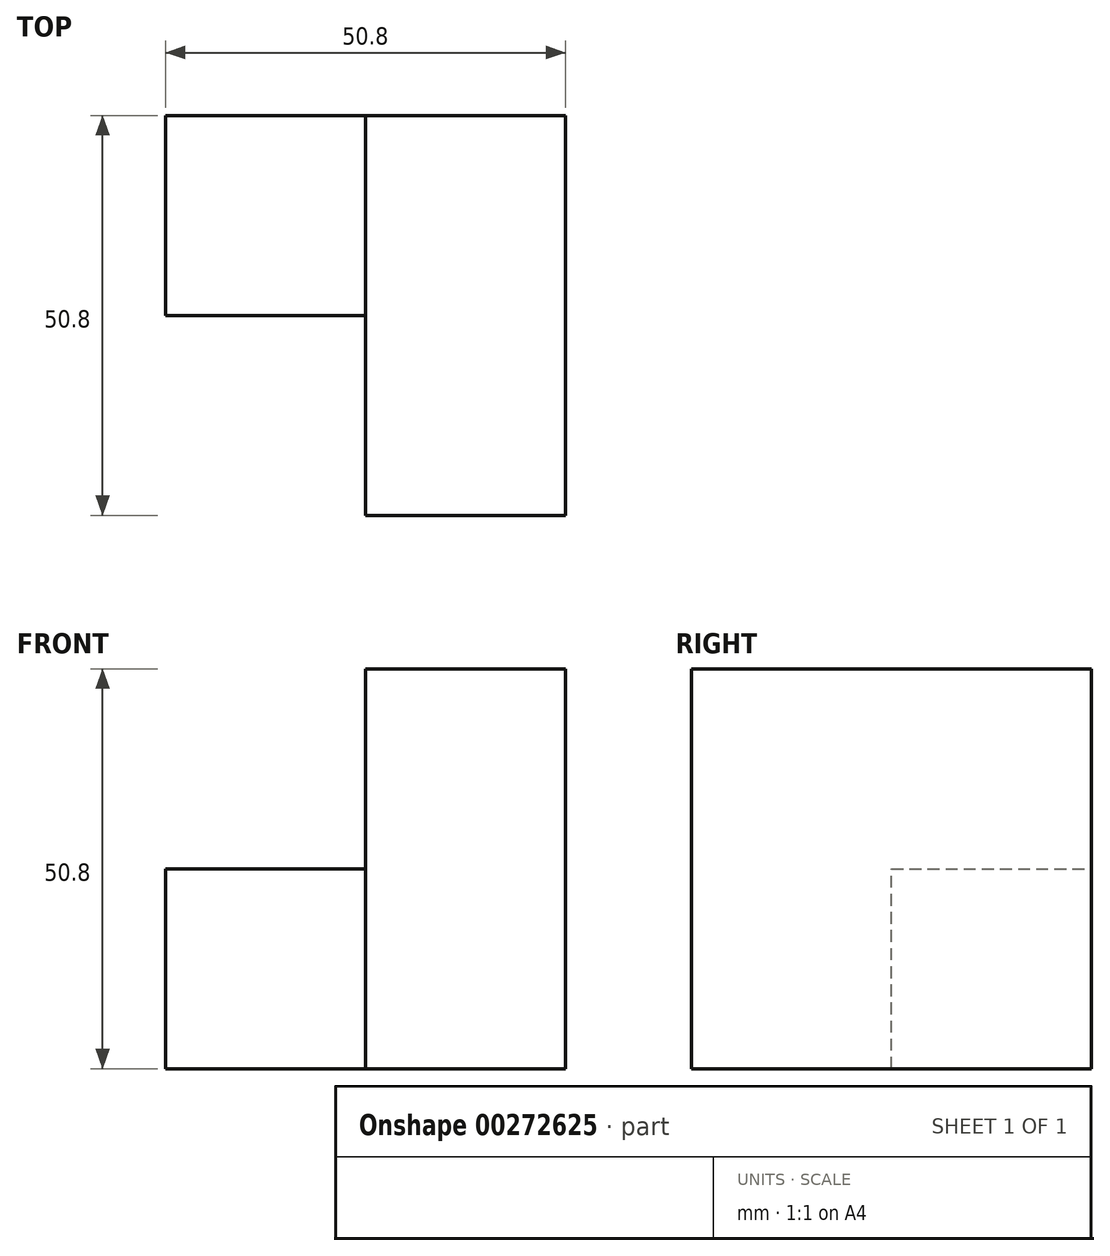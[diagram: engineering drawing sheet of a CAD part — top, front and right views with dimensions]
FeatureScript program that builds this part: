
annotation { "Feature Type Name" : "Feature", "Feature Type Description" : "" }
export const myFeature = defineFeature(function(context is Context, id is Id, definition is map)
    precondition{}
    {
        {
            var Q0;
            Q0=qCreatedBy(makeId("Front.planeOp"),FACE);
            var sketch = newSketch(context, id + "F0", { "sketchPlane" : qUnion([Q0])});
            skLineSegment(sketch, "E0", {"start": v(0, 0) * mm, "end": v(0, 50.8) * mm});
            skLineSegment(sketch, "E1", {"start": v(0, 0) * mm, "end": v(-25.4, 0) * mm});
            skLineSegment(sketch, "E2", {"start": v(-25.4, 0) * mm, "end": v(-25.4, 50.8) * mm});
            skLineSegment(sketch, "E3", {"start": v(0, 50.8) * mm, "end": v(-25.4, 50.8) * mm});
            skSolve(sketch);
        }
        {
            var Q0;
            Q0 = qSketchRegion(id + "F0", true);
            extrude(context, id + "F1", {"entities" : qUnion([Q0]), "depth" : 50.8 * mm});
        }
        {
            var Q0;
            Q0=makeQuery(id+"F1.opExtrude","SWEPT_FACE",FACE,{"disambiguationData":[OSD([sQuery(id+"F0.wireOp",EDGE,"E2")])]});
            var sketch = newSketch(context, id + "F2", { "sketchPlane" : qUnion([Q0])});
            skLineSegment(sketch, "E4", {"start": v(0, 0) * mm, "end": v(25.4, 0) * mm});
            skLineSegment(sketch, "E5", {"start": v(25.4, 0) * mm, "end": v(25.4, 25.4) * mm});
            skLineSegment(sketch, "E6", {"start": v(25.4, 25.4) * mm, "end": v(0, 25.4) * mm});
            skLineSegment(sketch, "E7", {"start": v(0, 0) * mm, "end": v(0, 25.4) * mm});
            skSolve(sketch);
        }
        {
            var Q0;
            Q0 = qSketchRegion(id + "F2", true);
            extrude(context, id + "F3", {"entities" : qUnion([Q0]), "operationType" : NewBodyOperationType.ADD, "depth" : 25.4 * mm});
        }
    });
